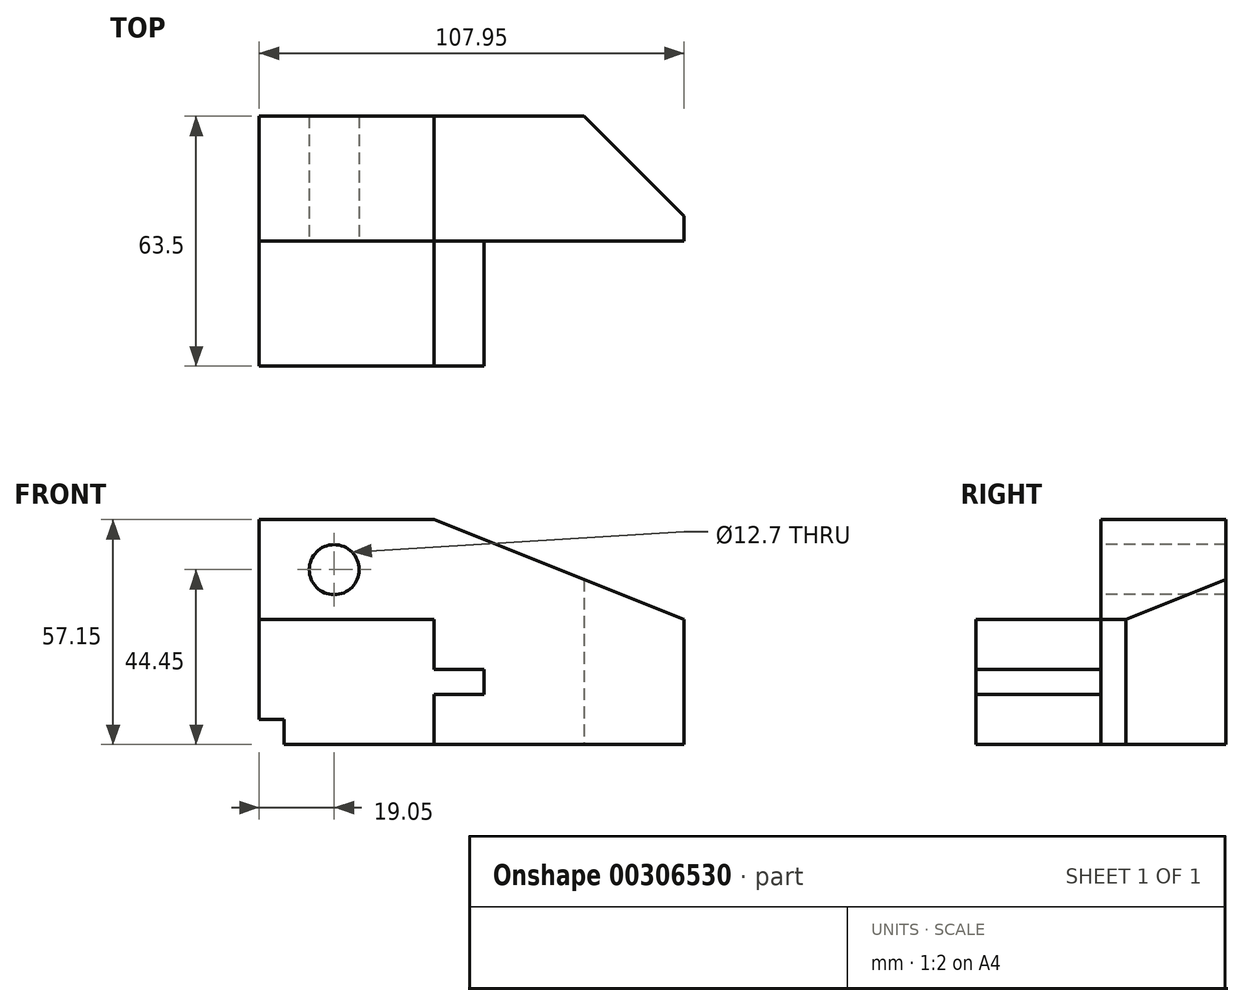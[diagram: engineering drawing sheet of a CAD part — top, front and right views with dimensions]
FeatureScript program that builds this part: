
annotation { "Feature Type Name" : "Feature", "Feature Type Description" : "" }
export const myFeature = defineFeature(function(context is Context, id is Id, definition is map)
    precondition{}
    {
        {
            var Q0;
            Q0=qCreatedBy(makeId("Top.planeOp"),FACE);
            var sketch = newSketch(context, id + "F0", { "sketchPlane" : qUnion([Q0])});
            skLineSegment(sketch, "E0.bottom", {"start": v(0, 0) * mm, "end": v(107.95, 0) * mm});
            skLineSegment(sketch, "E0.top", {"start": v(0, 63.5) * mm, "end": v(107.95, 63.5) * mm});
            skLineSegment(sketch, "E0.left", {"start": v(0, 0) * mm, "end": v(0, 63.5) * mm});
            skLineSegment(sketch, "E0.right", {"start": v(107.95, 0) * mm, "end": v(107.95, 63.5) * mm});
            skSolve(sketch);
        }
        {
            var Q0;
            Q0 = qSketchRegion(id + "F0", true);
            extrude(context, id + "F1", {"entities" : qUnion([Q0]), "depth" : 57.15 * mm});
        }
        {
            var Q0;
            Q0=makeQuery(id+"F1.opExtrude","SWEPT_FACE",FACE,{"disambiguationData":[OSD([sQuery(id+"F0.wireOp",EDGE,"E0.left")])]});
            var sketch = newSketch(context, id + "F2", { "sketchPlane" : qUnion([Q0])});
            skLineSegment(sketch, "E1", {"start": v(-31.75, 57.15) * mm, "end": v(-31.75, 31.75) * mm});
            skLineSegment(sketch, "E2", {"start": v(-31.75, 31.75) * mm, "end": v(0, 31.75) * mm});
            skLineSegment(sketch, "E3", {"start": v(0, 31.75) * mm, "end": v(0, 57.15) * mm});
            skLineSegment(sketch, "E4", {"start": v(0, 57.15) * mm, "end": v(-31.75, 57.15) * mm});
            skSolve(sketch);
        }
        {
            var Q0;
            Q0 = qSketchRegion(id + "F2", true);
            extrude(context, id + "F3", {"entities" : qUnion([Q0]), "operationType" : NewBodyOperationType.REMOVE, "endBound" : BoundingType.THROUGH_ALL, "oppositeDirection" : true, "depth" : 38.1 * mm});
        }
        {
            var Q0;
            Q0=makeQuery(id+"F1.opExtrude","SWEPT_FACE",FACE,{"disambiguationData":[OSD([sQuery(id+"F0.wireOp",EDGE,"E0.right")])]});
            var sketch = newSketch(context, id + "F4", { "sketchPlane" : qUnion([Q0])});
            skLineSegment(sketch, "E5", {"start": v(0, 19.05) * mm, "end": v(31.75, 19.05) * mm});
            skLineSegment(sketch, "E6", {"start": v(31.75, 19.05) * mm, "end": v(31.75, 31.75) * mm});
            skLineSegment(sketch, "E7", {"start": v(31.75, 31.75) * mm, "end": v(0, 31.75) * mm});
            skLineSegment(sketch, "E8", {"start": v(0, 31.75) * mm, "end": v(0, 19.05) * mm});
            skLineSegment(sketch, "E9", {"start": v(0, 12.7) * mm, "end": v(31.75, 12.7) * mm});
            skLineSegment(sketch, "E10", {"start": v(31.75, 12.7) * mm, "end": v(31.75, 0) * mm});
            skLineSegment(sketch, "E11", {"start": v(31.75, 0) * mm, "end": v(0, 0) * mm});
            skLineSegment(sketch, "E12", {"start": v(0, 0) * mm, "end": v(0, 12.7) * mm});
            skSolve(sketch);
        }
        {
            var Q0;
            Q0 = qSketchRegion(id + "F4", true);
            extrude(context, id + "F5", {"entities" : qUnion([Q0]), "operationType" : NewBodyOperationType.REMOVE, "oppositeDirection" : true, "depth" : 63.5 * mm});
        }
        {
            var Q0;
            Q0=makeQuery(id+"F5.boolean.opBoolean","COPY",FACE,{"derivedFrom":makeQuery(id+"F5.opExtrude","SWEPT_FACE",FACE,{"disambiguationData":[OSD([sQuery(id+"F4.wireOp",EDGE,"E5")])]})});
            var sketch = newSketch(context, id + "F6", { "sketchPlane" : qUnion([Q0])});
            skLineSegment(sketch, "E13", {"start": v(57.15, 31.75) * mm, "end": v(57.15, 0) * mm});
            skLineSegment(sketch, "E14", {"start": v(57.15, 0) * mm, "end": v(107.95, 0) * mm});
            skLineSegment(sketch, "E15", {"start": v(107.95, 0) * mm, "end": v(107.95, 31.75) * mm});
            skLineSegment(sketch, "E16", {"start": v(107.95, 31.75) * mm, "end": v(57.15, 31.75) * mm});
            skSolve(sketch);
        }
        {
            var Q0;
            Q0 = qSketchRegion(id + "F6", true);
            extrude(context, id + "F7", {"entities" : qUnion([Q0]), "operationType" : NewBodyOperationType.REMOVE, "oppositeDirection" : true, "depth" : 25.4 * mm});
        }
        {
            var Q0;
            Q0=makeQuery(id+"F7.boolean.opBoolean","MERGE",FACE,{"derivedFrom":[makeQuery(id+"F5.boolean.opBoolean","MERGE",FACE,{"derivedFrom":[makeQuery(id+"F3.boolean.opBoolean","COPY",FACE,{"derivedFrom":makeQuery(id+"F3.opExtrude","SWEPT_FACE",FACE,{"disambiguationData":[OSD([sQuery(id+"F2.wireOp",EDGE,"E1")])]})}),makeQuery(id+"F5.opExtrude","SWEPT_FACE",FACE,{"disambiguationData":[OSD([sQuery(id+"F4.wireOp",EDGE,"E6")])]})]}),makeQuery(id+"F5.boolean.opBoolean","COPY",FACE,{"derivedFrom":makeQuery(id+"F5.opExtrude","SWEPT_FACE",FACE,{"disambiguationData":[OSD([sQuery(id+"F4.wireOp",EDGE,"E10")])]})}),makeQuery(id+"F7.opExtrude","SWEPT_FACE",FACE,{"disambiguationData":[OSD([sQuery(id+"F6.wireOp",EDGE,"E16")])]})]});
            var sketch = newSketch(context, id + "F8", { "sketchPlane" : qUnion([Q0])});
            skCircle(sketch, "E17", {"center": v(19.05, 44.45) * mm, "radius": 6.35 * mm});
            skSolve(sketch);
        }
        {
            var Q0;
            Q0 = qSketchRegion(id + "F8", true);
            extrude(context, id + "F9", {"entities" : qUnion([Q0]), "operationType" : NewBodyOperationType.REMOVE, "endBound" : BoundingType.THROUGH_ALL, "oppositeDirection" : true, "depth" : 25.4 * mm});
        }
        {
            var Q0;
            Q0=makeQuery(id+"F1.opExtrude","SWEPT_FACE",FACE,{"disambiguationData":[OSD([sQuery(id+"F0.wireOp",EDGE,"E0.bottom")])]});
            var sketch = newSketch(context, id + "F10", { "sketchPlane" : qUnion([Q0])});
            skLineSegment(sketch, "E18", {"start": v(0, 6.35) * mm, "end": v(6.35, 6.35) * mm});
            skLineSegment(sketch, "E19", {"start": v(6.35, 6.35) * mm, "end": v(6.35, 0) * mm});
            skLineSegment(sketch, "E20", {"start": v(6.35, 0) * mm, "end": v(0, 0) * mm});
            skLineSegment(sketch, "E21", {"start": v(0, 0) * mm, "end": v(0, 6.35) * mm});
            skSolve(sketch);
        }
        {
            var Q0;
            Q0 = qSketchRegion(id + "F10", true);
            extrude(context, id + "F11", {"entities" : qUnion([Q0]), "operationType" : NewBodyOperationType.REMOVE, "endBound" : BoundingType.THROUGH_ALL, "oppositeDirection" : true, "depth" : 25.4 * mm});
        }
        {
            var Q0;
            Q0=makeQuery(id+"F7.boolean.opBoolean","MERGE",FACE,{"derivedFrom":[makeQuery(id+"F5.boolean.opBoolean","MERGE",FACE,{"derivedFrom":[makeQuery(id+"F3.boolean.opBoolean","COPY",FACE,{"derivedFrom":makeQuery(id+"F3.opExtrude","SWEPT_FACE",FACE,{"disambiguationData":[OSD([sQuery(id+"F2.wireOp",EDGE,"E1")])]})}),makeQuery(id+"F5.opExtrude","SWEPT_FACE",FACE,{"disambiguationData":[OSD([sQuery(id+"F4.wireOp",EDGE,"E6")])]})]}),makeQuery(id+"F5.boolean.opBoolean","COPY",FACE,{"derivedFrom":makeQuery(id+"F5.opExtrude","SWEPT_FACE",FACE,{"disambiguationData":[OSD([sQuery(id+"F4.wireOp",EDGE,"E10")])]})}),makeQuery(id+"F7.opExtrude","SWEPT_FACE",FACE,{"disambiguationData":[OSD([sQuery(id+"F6.wireOp",EDGE,"E16")])]})]});
            var sketch = newSketch(context, id + "F12", { "sketchPlane" : qUnion([Q0])});
            skLineSegment(sketch, "E22", {"start": v(44.45, 57.15) * mm, "end": v(107.95, 57.15) * mm});
            skLineSegment(sketch, "E23", {"start": v(107.95, 57.15) * mm, "end": v(107.95, 31.75) * mm});
            skLineSegment(sketch, "E24", {"start": v(107.95, 31.75) * mm, "end": v(44.45, 57.15) * mm});
            skSolve(sketch);
        }
        {
            var Q0;
            Q0 = qSketchRegion(id + "F12", true);
            extrude(context, id + "F13", {"entities" : qUnion([Q0]), "operationType" : NewBodyOperationType.REMOVE, "endBound" : BoundingType.THROUGH_ALL, "oppositeDirection" : true, "depth" : 25.4 * mm});
        }
        {
            var Q0;
            Q0=makeQuery(id+"F0.imprint","IMPRINT",FACE,{"disambiguationData":[TD([[makeQuery(id+"F0.imprint","IMPRINT",EDGE,{"derivedFrom":sQuery(id+"F0.wireOp",EDGE,"E0.bottom")}),1.0]])]});
            var sketch = newSketch(context, id + "F14", { "sketchPlane" : qUnion([Q0])});
            skLineSegment(sketch, "E25", {"start": v(107.95, 38.1) * mm, "end": v(107.95, 63.5) * mm});
            skLineSegment(sketch, "E26", {"start": v(107.95, 63.5) * mm, "end": v(82.55, 63.5) * mm});
            skLineSegment(sketch, "E27", {"start": v(82.55, 63.5) * mm, "end": v(107.95, 38.1) * mm});
            skSolve(sketch);
        }
        {
            var Q0;
            Q0 = qSketchRegion(id + "F14", true);
            extrude(context, id + "F15", {"entities" : qUnion([Q0]), "operationType" : NewBodyOperationType.REMOVE, "endBound" : BoundingType.THROUGH_ALL, "depth" : 25.4 * mm});
        }
    });
